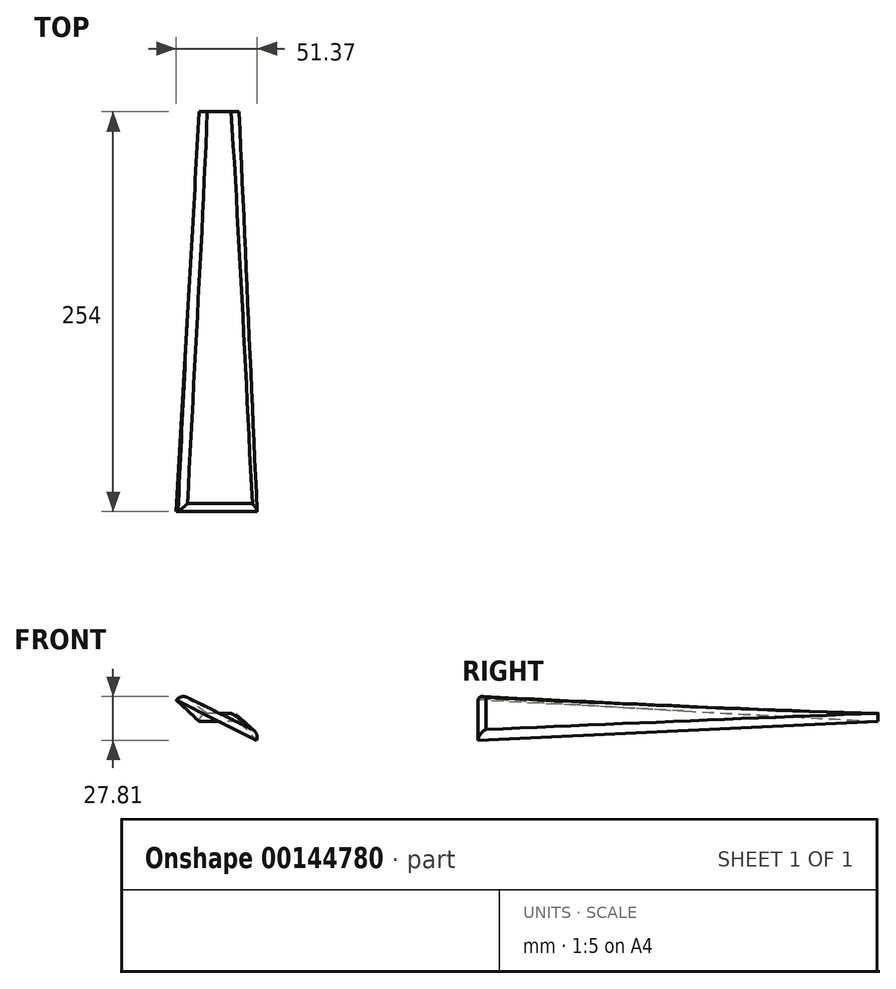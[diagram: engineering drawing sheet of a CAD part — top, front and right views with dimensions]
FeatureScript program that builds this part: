
annotation { "Feature Type Name" : "Feature", "Feature Type Description" : "" }
export const myFeature = defineFeature(function(context is Context, id is Id, definition is map)
    precondition{}
    {
        {
            var Q0;
            Q0=qCreatedBy(makeId("Front.planeOp"),FACE);
            var sketch = newSketch(context, id + "F0", { "sketchPlane" : qUnion([Q0])});
            skLineSegment(sketch, "E0.bottom", {"start": v(12.7, 2.54) * mm, "end": v(-12.7, 2.54) * mm});
            skLineSegment(sketch, "E0.top", {"start": v(12.7, -2.54) * mm, "end": v(-12.7, -2.54) * mm});
            skLineSegment(sketch, "E0.left", {"start": v(12.7, 2.54) * mm, "end": v(12.7, -2.54) * mm});
            skLineSegment(sketch, "E0.right", {"start": v(-12.7, 2.54) * mm, "end": v(-12.7, -2.54) * mm});
            skPoint(sketch, "E0.middle", {"position": v(0, 0) * mm});
            skSolve(sketch);
        }
        {
            var Q0;
            Q0=qCreatedBy(makeId("Front.planeOp"),FACE);
            cPlane(context, id + "F1", {"entities" : qUnion([Q0]), "cplaneType" : CPlaneType.OFFSET, "offset" : 254 * mm, "width" : 152.4 * mm, "height" : 152.4 * mm});
        }
        {
            var Q0;
            Q0=qCreatedBy(id+"F1.planeOp",FACE);
            var sketch = newSketch(context, id + "F2", { "sketchPlane" : qUnion([Q0])});
            skLineSegment(sketch, "E1", {"start": v(0, 0) * mm, "end": v(25.4, 0) * mm, "construction": true});
            skLineSegment(sketch, "E2", {"start": v(0, 0) * mm, "end": v(-25.4, 0) * mm, "construction": true});
            skLineSegment(sketch, "E3", {"start": v(-25.4, 0) * mm, "end": v(-25.4, 12.7) * mm, "construction": true});
            skLineSegment(sketch, "E4", {"start": v(25.4, 0) * mm, "end": v(25.4, -12.7) * mm, "construction": true});
            skLineSegment(sketch, "E5.bottom", {"start": v(-23.52, 10.99) * mm, "end": v(-27.28, 10.99) * mm, "construction": true});
            skLineSegment(sketch, "E5.top", {"start": v(-23.52, 14.41) * mm, "end": v(-27.28, 14.41) * mm, "construction": true});
            skLineSegment(sketch, "E5.left", {"start": v(-23.52, 10.99) * mm, "end": v(-23.52, 14.41) * mm, "construction": true});
            skLineSegment(sketch, "E5.right", {"start": v(-27.28, 10.99) * mm, "end": v(-27.28, 14.41) * mm, "construction": true});
            skPoint(sketch, "E5.middle", {"position": v(-25.4, 12.7) * mm});
            skLineSegment(sketch, "E6.bottom", {"start": v(27.13, -10.84) * mm, "end": v(23.67, -10.84) * mm, "construction": true});
            skLineSegment(sketch, "E6.top", {"start": v(27.13, -14.56) * mm, "end": v(23.67, -14.56) * mm, "construction": true});
            skLineSegment(sketch, "E6.left", {"start": v(27.13, -10.84) * mm, "end": v(27.13, -14.56) * mm, "construction": true});
            skLineSegment(sketch, "E6.right", {"start": v(23.67, -10.84) * mm, "end": v(23.67, -14.56) * mm, "construction": true});
            skPoint(sketch, "E6.middle", {"position": v(25.4, -12.7) * mm});
            skLineSegment(sketch, "E7", {"start": v(-27.28, 10.99) * mm, "end": v(23.67, -14.56) * mm});
            skLineSegment(sketch, "E8", {"start": v(23.67, -14.56) * mm, "end": v(27.13, -10.84) * mm});
            skLineSegment(sketch, "E9", {"start": v(27.13, -10.84) * mm, "end": v(-23.52, 14.41) * mm});
            skLineSegment(sketch, "E10", {"start": v(-23.52, 14.41) * mm, "end": v(-27.28, 10.99) * mm});
            skSolve(sketch);
        }
        {
            var Q0;
            Q0=makeQuery(id+"F0.imprint","IMPRINT",FACE,{"disambiguationData":[TD([[makeQuery(id+"F0.imprint","IMPRINT",EDGE,{"derivedFrom":sQuery(id+"F0.wireOp",EDGE,"E0.bottom")}),1.0]])]});
            var Q1;
            Q1=makeQuery(id+"F2.imprint","IMPRINT",FACE,{"disambiguationData":[TD([[makeQuery(id+"F2.imprint","IMPRINT",EDGE,{"derivedFrom":sQuery(id+"F2.wireOp",EDGE,"E7")}),1.0]])]});
            loft(context, id + "F3", {"sheetProfilesArray" : [{ "sheetProfileEntities" : qUnion([Q0]) }, { "sheetProfileEntities" : qUnion([Q1]) }]});
        }
        {
            var Q0;
            Q0=makeQuery(id+"F3.opLoft","SWEPT_EDGE",EDGE,{"disambiguationData":[OSD([sQuery(id+"F0.wireOp",EDGE,"E0.bottom"),sQuery(id+"F0.wireOp",EDGE,"E0.left"),sQuery(id+"F2.wireOp",EDGE,"E8"),sQuery(id+"F2.wireOp",EDGE,"E9")])]});
            var Q1;
            Q1=makeQuery(id+"F3.opLoft","SWEPT_EDGE",EDGE,{"disambiguationData":[OSD([sQuery(id+"F0.wireOp",EDGE,"E0.bottom"),sQuery(id+"F0.wireOp",EDGE,"E0.right"),sQuery(id+"F2.wireOp",EDGE,"E9"),sQuery(id+"F2.wireOp",EDGE,"E10")])]});
            var Q2;
            Q2=makeQuery(id+"F3.opLoft","MID_CAP_EDGE",EDGE,{"disambiguationData":[OSD([sQuery(id+"F2.wireOp",EDGE,"E8"),sQuery(id+"F2.wireOp",EDGE,"E9"),sQuery(id+"F2.wireOp",EDGE,"E10")])],"capPos":1.0});
            fillet(context, id + "F4", {"entities" : qUnion([Q0, Q1, Q2]), "radius" : 5.08 * mm, "tangentPropagation" : true, "allowEdgeOverflow" : false});
        }
    });
